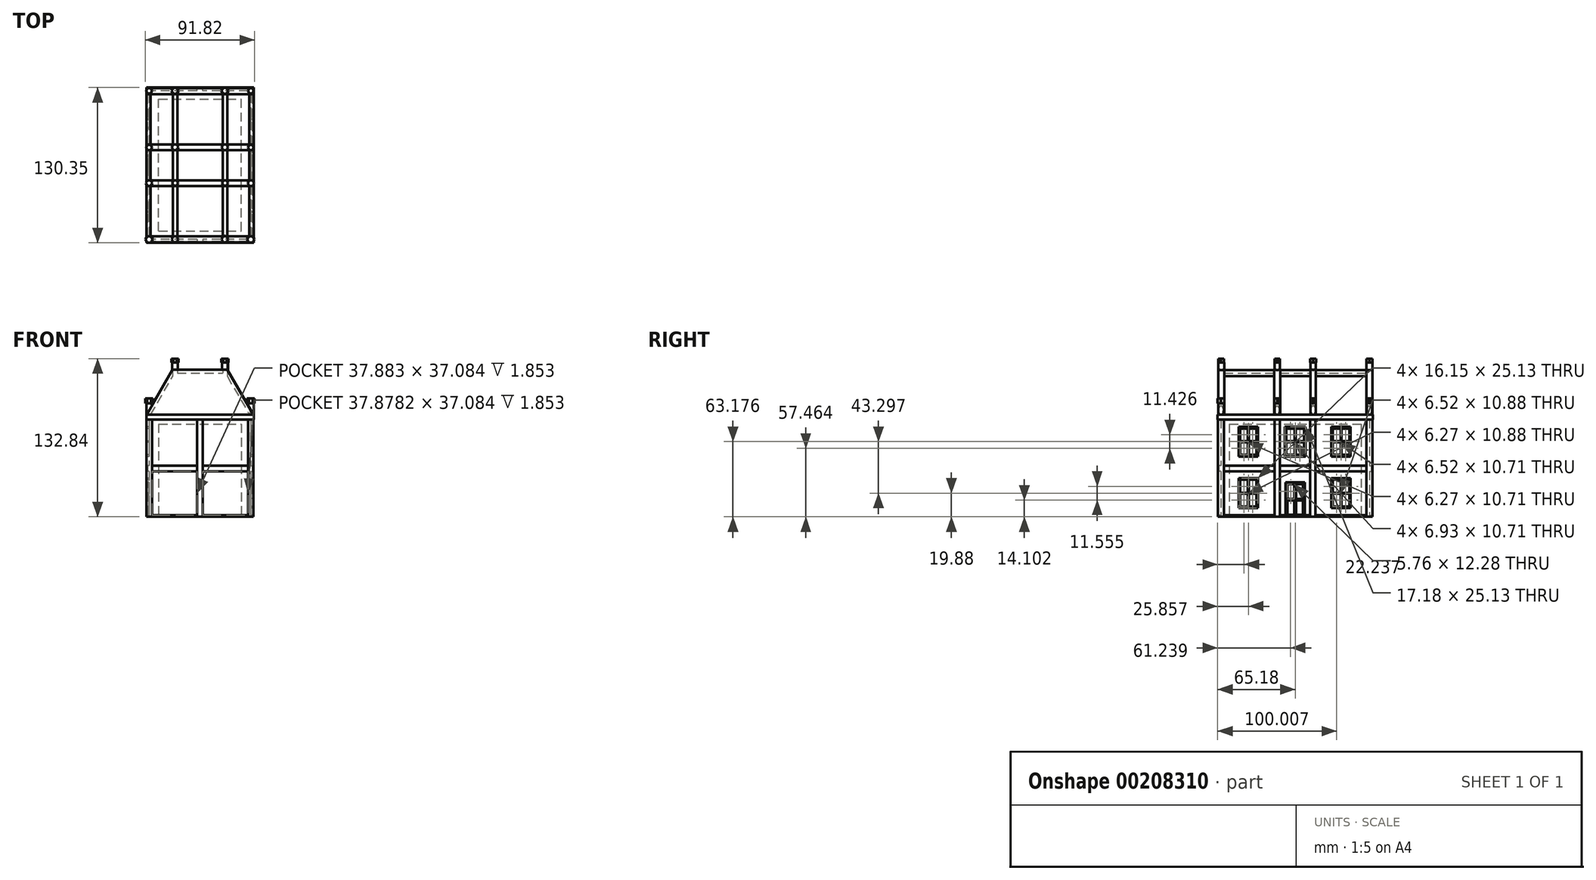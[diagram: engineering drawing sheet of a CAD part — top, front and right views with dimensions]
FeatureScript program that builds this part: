
annotation { "Feature Type Name" : "Feature", "Feature Type Description" : "" }
export const myFeature = defineFeature(function(context is Context, id is Id, definition is map)
    precondition{}
    {
        {
            var Q0;
            Q0=qCreatedBy(makeId("Top.planeOp"),FACE);
            var sketch = newSketch(context, id + "F0", { "sketchPlane" : qUnion([Q0])});
            skLineSegment(sketch, "E0.bottom", {"start": v(42.63, 62.44) * mm, "end": v(-42.63, 62.44) * mm});
            skLineSegment(sketch, "E0.top", {"start": v(42.63, -62.44) * mm, "end": v(-42.63, -62.44) * mm});
            skLineSegment(sketch, "E0.left", {"start": v(42.63, 62.44) * mm, "end": v(42.63, -62.44) * mm});
            skLineSegment(sketch, "E0.right", {"start": v(-42.63, 62.44) * mm, "end": v(-42.63, -62.44) * mm});
            skPoint(sketch, "E0.middle", {"position": v(0, 0) * mm});
            skLineSegment(sketch, "E1.bottom", {"start": v(40.33, -64.96) * mm, "end": v(44.94, -64.96) * mm});
            skLineSegment(sketch, "E1.top", {"start": v(40.33, -59.92) * mm, "end": v(44.94, -59.92) * mm});
            skLineSegment(sketch, "E1.left", {"start": v(40.33, -64.96) * mm, "end": v(40.33, -59.92) * mm});
            skLineSegment(sketch, "E1.right", {"start": v(44.94, -64.96) * mm, "end": v(44.94, -59.92) * mm});
            skPoint(sketch, "E1.middle", {"position": v(42.63, -62.44) * mm});
            skLineSegment(sketch, "E2.bottom", {"start": v(-40.33, -59.92) * mm, "end": v(-44.94, -59.92) * mm});
            skLineSegment(sketch, "E2.top", {"start": v(-40.33, -64.96) * mm, "end": v(-44.94, -64.96) * mm});
            skLineSegment(sketch, "E2.left", {"start": v(-40.33, -59.92) * mm, "end": v(-40.33, -64.96) * mm});
            skLineSegment(sketch, "E2.right", {"start": v(-44.94, -59.92) * mm, "end": v(-44.94, -64.96) * mm});
            skPoint(sketch, "E2.middle", {"position": v(-42.63, -62.44) * mm});
            skLineSegment(sketch, "E3.bottom", {"start": v(-40.33, 59.83) * mm, "end": v(-44.94, 59.83) * mm});
            skLineSegment(sketch, "E3.top", {"start": v(-40.33, 65.05) * mm, "end": v(-44.94, 65.05) * mm});
            skLineSegment(sketch, "E3.left", {"start": v(-40.33, 59.83) * mm, "end": v(-40.33, 65.05) * mm});
            skLineSegment(sketch, "E3.right", {"start": v(-44.94, 59.83) * mm, "end": v(-44.94, 65.05) * mm});
            skPoint(sketch, "E3.middle", {"position": v(-42.63, 62.44) * mm});
            skLineSegment(sketch, "E4.bottom", {"start": v(40.33, 59.83) * mm, "end": v(44.94, 59.83) * mm});
            skLineSegment(sketch, "E4.top", {"start": v(40.33, 65.05) * mm, "end": v(44.94, 65.05) * mm});
            skLineSegment(sketch, "E4.left", {"start": v(40.33, 59.83) * mm, "end": v(40.33, 65.05) * mm});
            skLineSegment(sketch, "E4.right", {"start": v(44.94, 59.83) * mm, "end": v(44.94, 65.05) * mm});
            skPoint(sketch, "E4.middle", {"position": v(42.63, 62.44) * mm});
            skLineSegment(sketch, "E5", {"start": v(40.33, -59.92) * mm, "end": v(0, 0) * mm});
            skLineSegment(sketch, "E6", {"start": v(40.33, 59.83) * mm, "end": v(0, 0) * mm});
            skLineSegment(sketch, "E7", {"start": v(-40.33, 59.83) * mm, "end": v(0, 0) * mm});
            skLineSegment(sketch, "E8", {"start": v(-40.33, -59.92) * mm, "end": v(0, 0) * mm});
            skLineSegment(sketch, "E9", {"start": v(20.16, -29.96) * mm, "end": v(-20.17, -29.96) * mm});
            skLineSegment(sketch, "E10", {"start": v(-20.17, -29.96) * mm, "end": v(-20.17, 29.92) * mm});
            skLineSegment(sketch, "E11", {"start": v(-20.17, 29.92) * mm, "end": v(20.16, 29.92) * mm});
            skLineSegment(sketch, "E12", {"start": v(20.16, 29.92) * mm, "end": v(20.16, -29.96) * mm});
            skPoint(sketch, "E13.middle", {"position": v(42.63, 29.92) * mm});
            skLineSegment(sketch, "E14.bottom", {"start": v(-2.45, -59.92) * mm, "end": v(2.45, -59.92) * mm});
            skLineSegment(sketch, "E14.top", {"start": v(-2.45, -64.96) * mm, "end": v(2.45, -64.96) * mm});
            skLineSegment(sketch, "E14.left", {"start": v(-2.45, -59.92) * mm, "end": v(-2.45, -64.96) * mm});
            skLineSegment(sketch, "E14.right", {"start": v(2.45, -59.92) * mm, "end": v(2.45, -64.96) * mm});
            skPoint(sketch, "E14.middle", {"position": v(0, -62.44) * mm});
            skLineSegment(sketch, "E15.bottom", {"start": v(2.45, 59.83) * mm, "end": v(-2.45, 59.83) * mm});
            skLineSegment(sketch, "E15.top", {"start": v(2.45, 65.05) * mm, "end": v(-2.45, 65.05) * mm});
            skLineSegment(sketch, "E15.left", {"start": v(2.45, 59.83) * mm, "end": v(2.45, 65.05) * mm});
            skLineSegment(sketch, "E15.right", {"start": v(-2.45, 59.83) * mm, "end": v(-2.45, 65.05) * mm});
            skPoint(sketch, "E15.middle", {"position": v(0, 62.44) * mm});
            skPoint(sketch, "E16.middle", {"position": v(-42.63, -29.96) * mm});
            skPoint(sketch, "E17.middle", {"position": v(-42.63, 29.92) * mm});
            skLineSegment(sketch, "E18.bottom", {"start": v(40.33, -17.25) * mm, "end": v(44.94, -17.25) * mm});
            skLineSegment(sketch, "E18.top", {"start": v(40.33, -12.94) * mm, "end": v(44.94, -12.94) * mm});
            skLineSegment(sketch, "E18.left", {"start": v(40.33, -17.25) * mm, "end": v(40.33, -12.94) * mm});
            skLineSegment(sketch, "E18.right", {"start": v(44.94, -17.25) * mm, "end": v(44.94, -12.94) * mm});
            skPoint(sketch, "E18.middle", {"position": v(42.63, -15.1) * mm});
            skLineSegment(sketch, "E19.bottom", {"start": v(40.33, 12.67) * mm, "end": v(44.94, 12.67) * mm});
            skLineSegment(sketch, "E19.top", {"start": v(40.33, 17.11) * mm, "end": v(44.94, 17.11) * mm});
            skLineSegment(sketch, "E19.left", {"start": v(40.33, 12.67) * mm, "end": v(40.33, 17.11) * mm});
            skLineSegment(sketch, "E19.right", {"start": v(44.94, 12.67) * mm, "end": v(44.94, 17.11) * mm});
            skPoint(sketch, "E19.middle", {"position": v(42.63, 14.9) * mm});
            skLineSegment(sketch, "E20.bottom", {"start": v(-40.33, -12.94) * mm, "end": v(-44.94, -12.94) * mm});
            skLineSegment(sketch, "E20.top", {"start": v(-40.33, -17.25) * mm, "end": v(-44.94, -17.25) * mm});
            skLineSegment(sketch, "E20.left", {"start": v(-40.33, -12.94) * mm, "end": v(-40.33, -17.25) * mm});
            skLineSegment(sketch, "E20.right", {"start": v(-44.94, -12.94) * mm, "end": v(-44.94, -17.25) * mm});
            skPoint(sketch, "E20.middle", {"position": v(-42.63, -15.1) * mm});
            skLineSegment(sketch, "E21.bottom", {"start": v(-40.33, 17.11) * mm, "end": v(-44.94, 17.11) * mm});
            skLineSegment(sketch, "E21.top", {"start": v(-40.33, 12.67) * mm, "end": v(-44.94, 12.67) * mm});
            skLineSegment(sketch, "E21.left", {"start": v(-40.33, 17.11) * mm, "end": v(-40.33, 12.67) * mm});
            skLineSegment(sketch, "E21.right", {"start": v(-44.94, 17.11) * mm, "end": v(-44.94, 12.67) * mm});
            skPoint(sketch, "E21.middle", {"position": v(-42.63, 14.9) * mm});
            skPoint(sketch, "E21.middle.positionSnap0", {"position": v(40.33, 14.9) * mm});
            skPoint(sketch, "E21.centerSnap0", {"position": v(40.33, 14.9) * mm});
            skSolve(sketch);
        }
        {
            var Q0;
            Q0 = qSketchRegion(id + "F0", true);
            extrude(context, id + "F1", {"entities" : qUnion([Q0]), "depth" : 83.31 * mm});
        }
        {
            var Q0;
            Q0=qCreatedBy(makeId("Top.planeOp"),FACE);
            var sketch = newSketch(context, id + "F2", { "sketchPlane" : qUnion([Q0])});
            skLineSegment(sketch, "E22.bottom", {"start": v(44.7, 64.75) * mm, "end": v(-44.7, 64.75) * mm});
            skLineSegment(sketch, "E22.top", {"start": v(44.7, -64.75) * mm, "end": v(-44.7, -64.75) * mm});
            skLineSegment(sketch, "E22.left", {"start": v(44.7, 64.75) * mm, "end": v(44.7, -64.75) * mm});
            skLineSegment(sketch, "E22.right", {"start": v(-44.7, 64.75) * mm, "end": v(-44.7, -64.75) * mm});
            skPoint(sketch, "E22.middle", {"position": v(0, 0) * mm});
            skSolve(sketch);
        }
        {
            var Q0;
            Q0 = qSketchRegion(id + "F2", true);
            extrude(context, id + "F3", {"entities" : qUnion([Q0]), "operationType" : NewBodyOperationType.ADD, "depth" : 1.27 * mm});
        }
        {
            var Q0;
            Q0=qCreatedBy(makeId("Top.planeOp"),FACE);
            cPlane(context, id + "F4", {"entities" : qUnion([Q0]), "cplaneType" : CPlaneType.OFFSET, "offset" : 40.64 * mm, "width" : 152.4 * mm, "height" : 152.4 * mm});
        }
        {
            var Q0;
            Q0=qCreatedBy(id+"F4.planeOp",FACE);
            var sketch = newSketch(context, id + "F5", { "sketchPlane" : qUnion([Q0])});
            skLineSegment(sketch, "E23.bottom", {"start": v(44.15, -64.3) * mm, "end": v(-44.15, -64.3) * mm});
            skLineSegment(sketch, "E23.top", {"start": v(44.15, 64.3) * mm, "end": v(-44.15, 64.3) * mm});
            skLineSegment(sketch, "E23.left", {"start": v(44.15, -64.3) * mm, "end": v(44.15, 64.3) * mm});
            skLineSegment(sketch, "E23.right", {"start": v(-44.15, -64.3) * mm, "end": v(-44.15, 64.3) * mm});
            skPoint(sketch, "E23.middle", {"position": v(0, 0) * mm});
            skSolve(sketch);
        }
        {
            var Q0;
            Q0 = qSketchRegion(id + "F5", true);
            extrude(context, id + "F6", {"entities" : qUnion([Q0]), "operationType" : NewBodyOperationType.ADD, "endBound" : BoundingType.SYMMETRIC, "depth" : 4.57 * mm});
        }
        {
            var Q0;
            Q0=qCreatedBy(makeId("Right.planeOp"),FACE);
            var sketch = newSketch(context, id + "F7", { "sketchPlane" : qUnion([Q0])});
            skLineSegment(sketch, "E24.bottom", {"start": v(30.45, 32.44) * mm, "end": v(46.6, 32.44) * mm});
            skLineSegment(sketch, "E24.top", {"start": v(30.45, 7.32) * mm, "end": v(46.6, 7.32) * mm});
            skLineSegment(sketch, "E24.left", {"start": v(30.45, 32.44) * mm, "end": v(30.45, 7.32) * mm});
            skLineSegment(sketch, "E24.right", {"start": v(46.6, 32.44) * mm, "end": v(46.6, 7.32) * mm});
            skPoint(sketch, "E24.middle", {"position": v(38.52, 19.88) * mm});
            skLineSegment(sketch, "E25.bottom", {"start": v(-31.25, 32.44) * mm, "end": v(-47.4, 32.44) * mm});
            skLineSegment(sketch, "E25.top", {"start": v(-31.25, 7.32) * mm, "end": v(-47.4, 7.32) * mm});
            skLineSegment(sketch, "E25.left", {"start": v(-31.25, 32.44) * mm, "end": v(-31.25, 7.32) * mm});
            skLineSegment(sketch, "E25.right", {"start": v(-47.4, 32.44) * mm, "end": v(-47.4, 7.32) * mm});
            skPoint(sketch, "E25.middle", {"position": v(-39.32, 19.88) * mm});
            skLineSegment(sketch, "E26.bottom", {"start": v(30.45, 75.74) * mm, "end": v(46.6, 75.74) * mm});
            skLineSegment(sketch, "E26.top", {"start": v(30.45, 50.61) * mm, "end": v(46.6, 50.61) * mm});
            skLineSegment(sketch, "E26.left", {"start": v(30.45, 75.74) * mm, "end": v(30.45, 50.61) * mm});
            skLineSegment(sketch, "E26.right", {"start": v(46.6, 75.74) * mm, "end": v(46.6, 50.61) * mm});
            skPoint(sketch, "E26.middle", {"position": v(38.52, 63.18) * mm});
            skPoint(sketch, "E26.cornerSnap0", {"position": v(30.45, 19.88) * mm});
            skLineSegment(sketch, "E27.bottom", {"start": v(-31.25, 50.61) * mm, "end": v(-47.4, 50.61) * mm});
            skLineSegment(sketch, "E27.top", {"start": v(-31.25, 75.74) * mm, "end": v(-47.4, 75.74) * mm});
            skLineSegment(sketch, "E27.left", {"start": v(-31.25, 50.61) * mm, "end": v(-31.25, 75.74) * mm});
            skLineSegment(sketch, "E27.right", {"start": v(-47.4, 50.61) * mm, "end": v(-47.4, 75.74) * mm});
            skPoint(sketch, "E27.middle", {"position": v(-39.32, 63.18) * mm});
            skPoint(sketch, "E27.middle.positionSnap0", {"position": v(-39.32, 32.44) * mm});
            skPoint(sketch, "E27.centerSnap0", {"position": v(-39.32, 32.44) * mm});
            skLineSegment(sketch, "E28.bottom", {"start": v(-8.59, 50.61) * mm, "end": v(8.59, 50.61) * mm});
            skLineSegment(sketch, "E28.top", {"start": v(-8.59, 75.74) * mm, "end": v(8.59, 75.74) * mm});
            skLineSegment(sketch, "E28.left", {"start": v(-8.59, 50.61) * mm, "end": v(-8.59, 75.74) * mm});
            skLineSegment(sketch, "E28.right", {"start": v(8.59, 50.61) * mm, "end": v(8.59, 75.74) * mm});
            skPoint(sketch, "E28.middle", {"position": v(0, 63.18) * mm});
            skLineSegment(sketch, "E29.left", {"start": v(-39.8, 8.66) * mm, "end": v(-39.8, 31.1) * mm});
            skLineSegment(sketch, "E29.right", {"start": v(-38.84, 8.66) * mm, "end": v(-38.84, 31.1) * mm});
            skLineSegment(sketch, "E30.left", {"start": v(-39.8, 52.1) * mm, "end": v(-39.8, 74.25) * mm});
            skLineSegment(sketch, "E30.right", {"start": v(-38.84, 52.1) * mm, "end": v(-38.84, 74.25) * mm});
            skLineSegment(sketch, "E31.left", {"start": v(-0.47, 52.1) * mm, "end": v(-0.47, 74.25) * mm});
            skLineSegment(sketch, "E31.right", {"start": v(0.47, 52.1) * mm, "end": v(0.47, 74.25) * mm});
            skLineSegment(sketch, "E32.left", {"start": v(38.09, 52.1) * mm, "end": v(38.09, 74.25) * mm});
            skLineSegment(sketch, "E32.right", {"start": v(38.96, 52.1) * mm, "end": v(38.96, 74.25) * mm});
            skLineSegment(sketch, "E33.left", {"start": v(38.96, 31.1) * mm, "end": v(38.96, 8.66) * mm});
            skLineSegment(sketch, "E33.right", {"start": v(38.09, 31.1) * mm, "end": v(38.09, 8.66) * mm});
            skLineSegment(sketch, "E34.bottom", {"start": v(31.57, 20.22) * mm, "end": v(45.48, 20.22) * mm});
            skLineSegment(sketch, "E35.bottom", {"start": v(-32.57, 20.22) * mm, "end": v(-46.08, 20.22) * mm});
            skLineSegment(sketch, "E36.bottom", {"start": v(-32.57, 63.53) * mm, "end": v(-46.08, 63.53) * mm});
            skLineSegment(sketch, "E37.bottom", {"start": v(-7.4, 63.53) * mm, "end": v(7.4, 63.53) * mm});
            skLineSegment(sketch, "E38.bottom", {"start": v(31.57, 63.53) * mm, "end": v(45.48, 63.53) * mm});
            skLineSegment(sketch, "E39", {"start": v(-46.08, 19.54) * mm, "end": v(-46.08, 8.66) * mm});
            skLineSegment(sketch, "E40", {"start": v(-32.57, 19.54) * mm, "end": v(-32.57, 8.66) * mm});
            skLineSegment(sketch, "E41", {"start": v(-32.57, 20.22) * mm, "end": v(-32.57, 31.1) * mm});
            skLineSegment(sketch, "E42", {"start": v(-46.08, 31.1) * mm, "end": v(-46.08, 20.22) * mm});
            skLineSegment(sketch, "E43", {"start": v(-32.57, 8.66) * mm, "end": v(-38.84, 8.66) * mm});
            skLineSegment(sketch, "E44", {"start": v(-39.8, 8.66) * mm, "end": v(-46.08, 8.66) * mm});
            skLineSegment(sketch, "E45", {"start": v(-32.57, 31.1) * mm, "end": v(-38.84, 31.1) * mm});
            skLineSegment(sketch, "E46", {"start": v(-39.8, 31.1) * mm, "end": v(-46.08, 31.1) * mm});
            skLineSegment(sketch, "E47", {"start": v(38.09, 8.66) * mm, "end": v(31.57, 8.66) * mm});
            skLineSegment(sketch, "E48", {"start": v(38.96, 8.66) * mm, "end": v(45.48, 8.66) * mm});
            skLineSegment(sketch, "E49", {"start": v(38.09, 31.1) * mm, "end": v(31.57, 31.1) * mm});
            skLineSegment(sketch, "E50", {"start": v(38.96, 31.1) * mm, "end": v(45.48, 31.1) * mm});
            skLineSegment(sketch, "E51", {"start": v(31.57, 31.1) * mm, "end": v(31.57, 20.22) * mm});
            skLineSegment(sketch, "E52", {"start": v(45.48, 20.22) * mm, "end": v(45.48, 31.1) * mm});
            skLineSegment(sketch, "E53", {"start": v(31.57, 19.54) * mm, "end": v(31.57, 8.66) * mm});
            skLineSegment(sketch, "E54", {"start": v(45.48, 8.66) * mm, "end": v(45.48, 19.54) * mm});
            skLineSegment(sketch, "E55", {"start": v(31.57, 19.54) * mm, "end": v(38.09, 19.54) * mm});
            skLineSegment(sketch, "E56", {"start": v(45.48, 19.54) * mm, "end": v(38.96, 19.54) * mm});
            skLineSegment(sketch, "E57", {"start": v(-46.08, 19.54) * mm, "end": v(-39.8, 19.54) * mm});
            skLineSegment(sketch, "E58", {"start": v(-32.57, 19.54) * mm, "end": v(-38.84, 19.54) * mm});
            skLineSegment(sketch, "E59", {"start": v(-46.08, 52.1) * mm, "end": v(-39.8, 52.1) * mm});
            skLineSegment(sketch, "E60", {"start": v(-38.84, 52.1) * mm, "end": v(-32.57, 52.1) * mm});
            skLineSegment(sketch, "E61", {"start": v(-7.4, 52.1) * mm, "end": v(-0.47, 52.1) * mm});
            skLineSegment(sketch, "E62", {"start": v(0.47, 52.1) * mm, "end": v(7.4, 52.1) * mm});
            skLineSegment(sketch, "E63", {"start": v(31.57, 52.1) * mm, "end": v(38.09, 52.1) * mm});
            skLineSegment(sketch, "E64", {"start": v(38.96, 52.1) * mm, "end": v(45.48, 52.1) * mm});
            skLineSegment(sketch, "E65", {"start": v(-46.08, 74.25) * mm, "end": v(-39.8, 74.25) * mm});
            skLineSegment(sketch, "E66", {"start": v(-38.84, 74.25) * mm, "end": v(-32.57, 74.25) * mm});
            skLineSegment(sketch, "E67", {"start": v(-7.4, 74.25) * mm, "end": v(-0.47, 74.25) * mm});
            skLineSegment(sketch, "E68", {"start": v(0.47, 74.25) * mm, "end": v(7.4, 74.25) * mm});
            skLineSegment(sketch, "E69", {"start": v(31.57, 74.25) * mm, "end": v(38.09, 74.25) * mm});
            skLineSegment(sketch, "E70", {"start": v(38.96, 74.25) * mm, "end": v(45.48, 74.25) * mm});
            skLineSegment(sketch, "E71", {"start": v(31.57, 62.82) * mm, "end": v(38.09, 62.82) * mm});
            skLineSegment(sketch, "E72", {"start": v(45.48, 62.82) * mm, "end": v(38.96, 62.82) * mm});
            skLineSegment(sketch, "E73", {"start": v(31.57, 74.25) * mm, "end": v(31.57, 63.53) * mm});
            skLineSegment(sketch, "E74", {"start": v(45.48, 74.25) * mm, "end": v(45.48, 63.53) * mm});
            skLineSegment(sketch, "E75", {"start": v(45.48, 52.1) * mm, "end": v(45.48, 62.82) * mm});
            skLineSegment(sketch, "E76", {"start": v(31.57, 62.82) * mm, "end": v(31.57, 52.1) * mm});
            skLineSegment(sketch, "E77", {"start": v(-7.4, 62.82) * mm, "end": v(-7.4, 52.1) * mm});
            skLineSegment(sketch, "E78", {"start": v(7.4, 52.1) * mm, "end": v(7.4, 62.82) * mm});
            skLineSegment(sketch, "E79", {"start": v(-7.4, 62.82) * mm, "end": v(-0.47, 62.82) * mm});
            skLineSegment(sketch, "E80", {"start": v(7.4, 62.82) * mm, "end": v(0.47, 62.82) * mm});
            skLineSegment(sketch, "E81", {"start": v(7.4, 63.53) * mm, "end": v(7.4, 74.25) * mm});
            skLineSegment(sketch, "E82", {"start": v(-7.4, 63.53) * mm, "end": v(-7.4, 74.25) * mm});
            skLineSegment(sketch, "E83", {"start": v(-46.08, 52.1) * mm, "end": v(-46.08, 62.82) * mm});
            skLineSegment(sketch, "E84", {"start": v(-32.57, 52.1) * mm, "end": v(-32.57, 62.82) * mm});
            skLineSegment(sketch, "E85", {"start": v(-32.57, 63.53) * mm, "end": v(-32.57, 74.25) * mm});
            skLineSegment(sketch, "E86", {"start": v(-46.08, 63.53) * mm, "end": v(-46.08, 74.25) * mm});
            skLineSegment(sketch, "E87", {"start": v(-46.08, 62.82) * mm, "end": v(-39.8, 62.82) * mm});
            skLineSegment(sketch, "E88", {"start": v(-32.57, 62.82) * mm, "end": v(-38.84, 62.82) * mm});
            skSolve(sketch);
        }
        {
            var Q0;
            Q0 = qSketchRegion(id + "F7", true);
            extrude(context, id + "F8", {"entities" : qUnion([Q0]), "operationType" : NewBodyOperationType.ADD, "endBound" : BoundingType.SYMMETRIC, "depth" : 89.4 * mm});
        }
        {
            var Q0;
            Q0 = qSketchRegion(id + "F7", true);
            extrude(context, id + "F9", {"entities" : qUnion([Q0]), "operationType" : NewBodyOperationType.ADD, "depth" : 25.4 * mm});
        }
        {
            var Q0;
            Q0 = qSketchRegion(id + "F7", true);
            extrude(context, id + "F10", {"entities" : qUnion([Q0]), "operationType" : NewBodyOperationType.ADD, "depth" : 25.4 * mm});
        }
        {
            var Q0;
            Q0=qCreatedBy(id+"F4.planeOp",FACE);
            cPlane(context, id + "F11", {"entities" : qUnion([Q0]), "cplaneType" : CPlaneType.OFFSET, "offset" : 43.18 * mm, "width" : 152.4 * mm, "height" : 152.4 * mm});
        }
        {
            var Q0;
            Q0=qCreatedBy(id+"F11.planeOp",FACE);
            var sketch = newSketch(context, id + "F12", { "sketchPlane" : qUnion([Q0])});
            skLineSegment(sketch, "E89.bottom", {"start": v(45.1, 65.17) * mm, "end": v(-45.1, 65.17) * mm});
            skLineSegment(sketch, "E89.top", {"start": v(45.1, -65.17) * mm, "end": v(-45.1, -65.17) * mm});
            skLineSegment(sketch, "E89.left", {"start": v(45.1, 65.17) * mm, "end": v(45.1, -65.17) * mm});
            skLineSegment(sketch, "E89.right", {"start": v(-45.1, 65.17) * mm, "end": v(-45.1, -65.17) * mm});
            skPoint(sketch, "E89.middle", {"position": v(0, 0) * mm});
            skSolve(sketch);
        }
        {
            var Q0;
            Q0 = qSketchRegion(id + "F12", true);
            extrude(context, id + "F13", {"entities" : qUnion([Q0]), "operationType" : NewBodyOperationType.ADD, "endBound" : BoundingType.SYMMETRIC, "depth" : 4.06 * mm});
        }
        {
            var Q0;
            Q0=qCreatedBy(makeId("Front.planeOp"),FACE);
            var sketch = newSketch(context, id + "F14", { "sketchPlane" : qUnion([Q0])});
            skCircle(sketch, "E90.cCircle", {"center": v(0, 83.84) * mm, "radius": 36.97 * mm, "construction": true});
            skLineSegment(sketch, "E90.0", {"start": v(21.35, 46.87) * mm, "end": v(-21.35, 46.87) * mm});
            skLineSegment(sketch, "E90.1", {"start": v(-21.35, 46.87) * mm, "end": v(-42.7, 83.84) * mm});
            skLineSegment(sketch, "E90.2", {"start": v(-42.7, 83.84) * mm, "end": v(-21.35, 120.82) * mm});
            skLineSegment(sketch, "E90.3", {"start": v(-21.35, 120.82) * mm, "end": v(21.35, 120.82) * mm});
            skLineSegment(sketch, "E90.4", {"start": v(21.35, 120.82) * mm, "end": v(42.7, 83.84) * mm});
            skLineSegment(sketch, "E90.5", {"start": v(42.7, 83.84) * mm, "end": v(21.35, 46.87) * mm});
            skPoint(sketch, "E90.0.midPoint", {"position": v(0, 46.87) * mm});
            skSolve(sketch);
        }
        {
            var Q0;
            Q0 = qSketchRegion(id + "F14", true);
            extrude(context, id + "F15", {"entities" : qUnion([Q0]), "operationType" : NewBodyOperationType.ADD, "endBound" : BoundingType.SYMMETRIC, "depth" : 123.95 * mm});
        }
        {
            var Q0;
            Q0=qCreatedBy(makeId("Front.planeOp"),FACE);
            cPlane(context, id + "F16", {"entities" : qUnion([Q0]), "cplaneType" : CPlaneType.OFFSET, "offset" : 64.77 * mm, "width" : 152.4 * mm, "height" : 152.4 * mm});
        }
        {
            var Q0;
            Q0=qCreatedBy(id+"F16.planeOp",FACE);
            var sketch = newSketch(context, id + "F17", { "sketchPlane" : qUnion([Q0])});
            skLineSegment(sketch, "E91.0", {"start": v(-22.93, 123.62) * mm, "end": v(22.93, 123.62) * mm});
            skLineSegment(sketch, "E91.1", {"start": v(22.93, 123.62) * mm, "end": v(45.85, 83.91) * mm});
            skLineSegment(sketch, "E91.5", {"start": v(-45.85, 83.91) * mm, "end": v(-22.93, 123.62) * mm});
            skPoint(sketch, "E91.0.midPoint", {"position": v(0, 123.62) * mm});
            skLineSegment(sketch, "E92", {"start": v(-44.92, 85.51) * mm, "end": v(44.92, 85.51) * mm});
            skSolve(sketch);
        }
        {
            var Q0;
            Q0 = qSketchRegion(id + "F17", true);
            extrude(context, id + "F18", {"entities" : qUnion([Q0]), "operationType" : NewBodyOperationType.ADD, "oppositeDirection" : true, "depth" : 5.08 * mm});
        }
        {
            var Q0;
            Q0=qCreatedBy(makeId("Front.planeOp"),FACE);
            cPlane(context, id + "F19", {"entities" : qUnion([Q0]), "cplaneType" : CPlaneType.OFFSET, "offset" : 64.77 * mm, "oppositeDirection" : true, "width" : 152.4 * mm, "height" : 152.4 * mm});
        }
        {
            var Q0;
            Q0=qCreatedBy(id+"F19.planeOp",FACE);
            var sketch = newSketch(context, id + "F20", { "sketchPlane" : qUnion([Q0])});
            skLineSegment(sketch, "E93.0", {"start": v(-22.98, 123.6) * mm, "end": v(22.98, 123.6) * mm});
            skLineSegment(sketch, "E93.1", {"start": v(22.98, 123.6) * mm, "end": v(45.96, 83.8) * mm});
            skLineSegment(sketch, "E93.5", {"start": v(-45.96, 83.8) * mm, "end": v(-22.98, 123.6) * mm});
            skPoint(sketch, "E93.0.midPoint", {"position": v(0, 123.6) * mm});
            skLineSegment(sketch, "E94", {"start": v(44.8, 85.82) * mm, "end": v(-44.8, 85.82) * mm});
            skSolve(sketch);
        }
        {
            var Q0;
            Q0 = qSketchRegion(id + "F20", true);
            extrude(context, id + "F21", {"entities" : qUnion([Q0]), "operationType" : NewBodyOperationType.ADD, "depth" : 5.08 * mm});
        }
        {
            var Q0;
            Q0=qCreatedBy(id+"F11.planeOp",FACE);
            cPlane(context, id + "F22", {"entities" : qUnion([Q0]), "cplaneType" : CPlaneType.OFFSET, "offset" : 39.37 * mm, "width" : 152.4 * mm, "height" : 152.4 * mm});
        }
        {
            var Q0;
            Q0=qCreatedBy(id+"F22.planeOp",FACE);
            var sketch = newSketch(context, id + "F23", { "sketchPlane" : qUnion([Q0])});
            skLineSegment(sketch, "E95.left", {"start": v(-22.88, -60) * mm, "end": v(-22.88, 60) * mm});
            skLineSegment(sketch, "E95.right", {"start": v(22.88, -60) * mm, "end": v(22.88, 60) * mm});
            skPoint(sketch, "E95.middle", {"position": v(0, 0) * mm});
            skLineSegment(sketch, "E96.left", {"start": v(-19.07, -60) * mm, "end": v(-19.07, 60) * mm});
            skLineSegment(sketch, "E96.right", {"start": v(19.07, -60) * mm, "end": v(19.07, 60) * mm});
            skLineSegment(sketch, "E97", {"start": v(22.88, -60) * mm, "end": v(19.07, -60) * mm});
            skLineSegment(sketch, "E98", {"start": v(22.88, 60) * mm, "end": v(19.07, 60) * mm});
            skLineSegment(sketch, "E99", {"start": v(-19.07, 60) * mm, "end": v(-22.88, 60) * mm});
            skLineSegment(sketch, "E100", {"start": v(-19.07, -60) * mm, "end": v(-22.88, -60) * mm});
            skSolve(sketch);
        }
        {
            var Q0;
            Q0 = qSketchRegion(id + "F23", true);
            extrude(context, id + "F24", {"entities" : qUnion([Q0]), "operationType" : NewBodyOperationType.ADD, "oppositeDirection" : true, "depth" : 1.02 * mm});
        }
        {
            var Q0;
            Q0 = qSketchRegion(id + "F23", true);
            extrude(context, id + "F25", {"entities" : qUnion([Q0]), "operationType" : NewBodyOperationType.ADD, "oppositeDirection" : true, "depth" : 12.45 * mm});
        }
        {
            var Q0;
            Q0=qCreatedBy(makeId("Front.planeOp"),FACE);
            cPlane(context, id + "F26", {"entities" : qUnion([Q0]), "cplaneType" : CPlaneType.OFFSET, "offset" : 17.53 * mm, "width" : 152.4 * mm, "height" : 152.4 * mm});
        }
        {
            var Q0;
            Q0=qCreatedBy(makeId("Front.planeOp"),FACE);
            cPlane(context, id + "F27", {"entities" : qUnion([Q0]), "cplaneType" : CPlaneType.OFFSET, "offset" : 17.27 * mm, "oppositeDirection" : true, "width" : 152.4 * mm, "height" : 152.4 * mm});
        }
        {
            var Q0;
            Q0=qCreatedBy(id+"F26.planeOp",FACE);
            var sketch = newSketch(context, id + "F28", { "sketchPlane" : qUnion([Q0])});
            skLineSegment(sketch, "E101.2", {"start": v(-45.74, 83.98) * mm, "end": v(-22.87, 123.6) * mm});
            skLineSegment(sketch, "E101.3", {"start": v(-22.87, 123.6) * mm, "end": v(22.87, 123.6) * mm});
            skLineSegment(sketch, "E101.4", {"start": v(22.87, 123.6) * mm, "end": v(45.74, 83.98) * mm});
            skPoint(sketch, "E101.0.midPoint", {"position": v(0, 44.37) * mm});
            skLineSegment(sketch, "E102", {"start": v(-44.65, 85.88) * mm, "end": v(44.65, 85.88) * mm});
            skSolve(sketch);
        }
        {
            var Q0;
            Q0 = qSketchRegion(id + "F28", true);
            extrude(context, id + "F29", {"entities" : qUnion([Q0]), "operationType" : NewBodyOperationType.ADD, "oppositeDirection" : true, "depth" : 4.83 * mm});
        }
        {
            var Q0;
            Q0=qCreatedBy(id+"F27.planeOp",FACE);
            var sketch = newSketch(context, id + "F30", { "sketchPlane" : qUnion([Q0])});
            skLineSegment(sketch, "E103.0", {"start": v(-22.98, 123.72) * mm, "end": v(22.98, 123.72) * mm});
            skLineSegment(sketch, "E103.1", {"start": v(22.98, 123.72) * mm, "end": v(45.96, 83.92) * mm});
            skPoint(sketch, "E103.0.midPoint", {"position": v(0, 123.72) * mm});
            skLineSegment(sketch, "E104", {"start": v(-44.95, 85.68) * mm, "end": v(44.95, 85.68) * mm});
            skLineSegment(sketch, "E105", {"start": v(-22.98, 123.72) * mm, "end": v(-44.95, 85.68) * mm});
            skSolve(sketch);
        }
        {
            var Q0;
            Q0 = qSketchRegion(id + "F30", true);
            extrude(context, id + "F31", {"entities" : qUnion([Q0]), "operationType" : NewBodyOperationType.ADD, "depth" : 4.57 * mm});
        }
        {
            var Q0;
            Q0=qCreatedBy(makeId("Right.planeOp"),FACE);
            var sketch = newSketch(context, id + "F32", { "sketchPlane" : qUnion([Q0])});
            skLineSegment(sketch, "E106.top", {"start": v(-8.16, 29.03) * mm, "end": v(8.16, 29.03) * mm});
            skLineSegment(sketch, "E106.left", {"start": v(-8.16, 1.21) * mm, "end": v(-8.16, 29.03) * mm});
            skLineSegment(sketch, "E106.right", {"start": v(8.16, 1.21) * mm, "end": v(8.16, 29.03) * mm});
            skPoint(sketch, "E106.middle", {"position": v(0, 15.12) * mm});
            skLineSegment(sketch, "E107.bottom", {"start": v(6.76, 27.86) * mm, "end": v(-6.76, 27.86) * mm});
            skLineSegment(sketch, "E107.left", {"start": v(6.76, 27.86) * mm, "end": v(6.76, 2.39) * mm});
            skLineSegment(sketch, "E107.right", {"start": v(-6.76, 27.86) * mm, "end": v(-6.76, 2.39) * mm});
            skLineSegment(sketch, "E108", {"start": v(6.76, 2.39) * mm, "end": v(6.76, 1.21) * mm});
            skLineSegment(sketch, "E109", {"start": v(6.76, 1.21) * mm, "end": v(8.16, 1.21) * mm});
            skLineSegment(sketch, "E110", {"start": v(-6.76, 2.39) * mm, "end": v(-6.76, 1.21) * mm});
            skLineSegment(sketch, "E111", {"start": v(-6.76, 1.21) * mm, "end": v(-8.16, 1.21) * mm});
            skSolve(sketch);
        }
        {
            var Q0;
            Q0 = qSketchRegion(id + "F32", true);
            extrude(context, id + "F33", {"entities" : qUnion([Q0]), "operationType" : NewBodyOperationType.ADD, "endBound" : BoundingType.SYMMETRIC, "depth" : 89.4 * mm});
        }
        {
            var Q0;
            Q0 = qSketchRegion(id + "F32", true);
            extrude(context, id + "F34", {"entities" : qUnion([Q0]), "operationType" : NewBodyOperationType.ADD, "depth" : 25.4 * mm});
        }
        {
            var Q0;
            Q0=qCreatedBy(makeId("Right.planeOp"),FACE);
            var sketch = newSketch(context, id + "F35", { "sketchPlane" : qUnion([Q0])});
            skLineSegment(sketch, "E112.bottom", {"start": v(-0.07, 1.25) * mm, "end": v(0.07, 1.25) * mm});
            skLineSegment(sketch, "E112.top", {"start": v(-0.07, 27.75) * mm, "end": v(0.07, 27.75) * mm});
            skLineSegment(sketch, "E112.left", {"start": v(-0.07, 1.25) * mm, "end": v(-0.07, 27.75) * mm});
            skLineSegment(sketch, "E112.right", {"start": v(0.07, 1.25) * mm, "end": v(0.07, 27.75) * mm});
            skPoint(sketch, "E112.middle", {"position": v(0, 14.5) * mm});
            skLineSegment(sketch, "E113.bottom", {"start": v(0.07, 27.9) * mm, "end": v(-0.07, 27.9) * mm});
            skLineSegment(sketch, "E113.top", {"start": v(0.07, 27.58) * mm, "end": v(-0.07, 27.58) * mm});
            skLineSegment(sketch, "E113.left", {"start": v(0.07, 27.9) * mm, "end": v(0.07, 27.58) * mm});
            skLineSegment(sketch, "E113.right", {"start": v(-0.07, 27.9) * mm, "end": v(-0.07, 27.58) * mm});
            skPoint(sketch, "E113.middle", {"position": v(0, 27.75) * mm});
            skLineSegment(sketch, "E114.bottom", {"start": v(-0.73, 14.5) * mm, "end": v(0.73, 14.5) * mm});
            skLineSegment(sketch, "E114.top", {"start": v(-0.73, 14.5) * mm, "end": v(0.73, 14.5) * mm});
            skLineSegment(sketch, "E114.left", {"start": v(-0.73, 14.5) * mm, "end": v(-0.73, 14.5) * mm});
            skLineSegment(sketch, "E114.right", {"start": v(0.73, 14.5) * mm, "end": v(0.73, 14.5) * mm});
            skCircle(sketch, "E115", {"center": v(-0.73, 14.5) * mm, "radius": 0.27 * mm});
            skCircle(sketch, "E116", {"center": v(0.73, 14.5) * mm, "radius": 0.27 * mm});
            skLineSegment(sketch, "E117.bottom", {"start": v(-6.5, 27.41) * mm, "end": v(-0.66, 27.41) * mm});
            skLineSegment(sketch, "E117.left", {"start": v(-6.5, 27.41) * mm, "end": v(-6.5, 15.13) * mm});
            skLineSegment(sketch, "E118.bottom", {"start": v(-6.5, 1.67) * mm, "end": v(-0.73, 1.67) * mm});
            skLineSegment(sketch, "E118.top", {"start": v(-6.5, 13.73) * mm, "end": v(-0.73, 13.73) * mm});
            skLineSegment(sketch, "E118.left", {"start": v(-6.5, 1.67) * mm, "end": v(-6.5, 13.73) * mm});
            skLineSegment(sketch, "E118.right", {"start": v(-0.73, 1.67) * mm, "end": v(-0.73, 13.73) * mm});
            skLineSegment(sketch, "E119.bottom", {"start": v(6.46, 27.41) * mm, "end": v(0.8, 27.41) * mm});
            skLineSegment(sketch, "E119.top", {"start": v(6.46, 15.13) * mm, "end": v(0.8, 15.13) * mm});
            skLineSegment(sketch, "E119.left", {"start": v(6.46, 27.41) * mm, "end": v(6.46, 15.13) * mm});
            skLineSegment(sketch, "E119.right", {"start": v(0.8, 27.41) * mm, "end": v(0.8, 15.13) * mm});
            skLineSegment(sketch, "E120.bottom", {"start": v(6.46, 1.67) * mm, "end": v(0.8, 1.67) * mm});
            skLineSegment(sketch, "E120.top", {"start": v(6.46, 13.73) * mm, "end": v(0.8, 13.73) * mm});
            skLineSegment(sketch, "E120.left", {"start": v(6.46, 1.67) * mm, "end": v(6.46, 13.73) * mm});
            skLineSegment(sketch, "E120.right", {"start": v(0.8, 1.67) * mm, "end": v(0.8, 13.73) * mm});
            skLineSegment(sketch, "E121.bottom", {"start": v(-6.5, 27.41) * mm, "end": v(-0.73, 27.41) * mm});
            skLineSegment(sketch, "E121.top", {"start": v(-6.5, 15.13) * mm, "end": v(-0.73, 15.13) * mm});
            skLineSegment(sketch, "E121.right", {"start": v(-0.73, 27.41) * mm, "end": v(-0.73, 15.13) * mm});
            skSolve(sketch);
        }
        {
            var Q0;
            Q0 = qSketchRegion(id + "F35", true);
            extrude(context, id + "F36", {"entities" : qUnion([Q0]), "operationType" : NewBodyOperationType.ADD, "endBound" : BoundingType.SYMMETRIC, "depth" : 85.85 * mm});
        }
        {
            var Q0;
            Q0=qCreatedBy(id+"F22.planeOp",FACE);
            var sketch = newSketch(context, id + "F37", { "sketchPlane" : qUnion([Q0])});
            skCircle(sketch, "E122", {"center": v(20.92, 62.33) * mm, "radius": 2.55 * mm});
            skCircle(sketch, "E123", {"center": v(-21.02, 62.33) * mm, "radius": 2.38 * mm});
            skCircle(sketch, "E124", {"center": v(-21.02, 15.02) * mm, "radius": 2.27 * mm});
            skCircle(sketch, "E125", {"center": v(20.92, 15.02) * mm, "radius": 2.2 * mm});
            skCircle(sketch, "E126", {"center": v(20.92, -15.14) * mm, "radius": 2.24 * mm});
            skCircle(sketch, "E127", {"center": v(-21.02, -15.14) * mm, "radius": 2.22 * mm});
            skCircle(sketch, "E128", {"center": v(20.92, -62.05) * mm, "radius": 2.45 * mm});
            skCircle(sketch, "E129", {"center": v(-21.02, -62.05) * mm, "radius": 2.35 * mm});
            skSolve(sketch);
        }
        {
            var Q0;
            Q0 = qSketchRegion(id + "F37", true);
            extrude(context, id + "F38", {"entities" : qUnion([Q0]), "operationType" : NewBodyOperationType.ADD, "depth" : 6.35 * mm});
        }
        {
            var Q0;
            Q0=qCreatedBy(id+"F11.planeOp",FACE);
            var sketch = newSketch(context, id + "F39", { "sketchPlane" : qUnion([Q0])});
            skPoint(sketch, "E130.middle", {"position": v(0, 0) * mm});
            skCircle(sketch, "E131", {"center": v(-42.74, -62.37) * mm, "radius": 2.2 * mm});
            skCircle(sketch, "E132", {"center": v(-42.74, -15.18) * mm, "radius": 2.24 * mm});
            skCircle(sketch, "E133", {"center": v(-42.74, 15.09) * mm, "radius": 2.15 * mm});
            skCircle(sketch, "E134", {"center": v(-42.74, 62.37) * mm, "radius": 2.27 * mm});
            skCircle(sketch, "E135", {"center": v(42.74, -62.37) * mm, "radius": 2.35 * mm});
            skCircle(sketch, "E136", {"center": v(42.74, -15.18) * mm, "radius": 2.26 * mm});
            skCircle(sketch, "E137", {"center": v(42.74, 15.09) * mm, "radius": 2.28 * mm});
            skCircle(sketch, "E138", {"center": v(42.74, 62.37) * mm, "radius": 2.25 * mm});
            skSolve(sketch);
        }
        {
            var Q0;
            Q0 = qSketchRegion(id + "F39", true);
            extrude(context, id + "F40", {"entities" : qUnion([Q0]), "operationType" : NewBodyOperationType.ADD, "depth" : 11.94 * mm});
        }
        {
            var Q0;
            Q0=qCreatedBy(id+"F11.planeOp",FACE);
            cPlane(context, id + "F41", {"entities" : qUnion([Q0]), "cplaneType" : CPlaneType.OFFSET, "offset" : 11.68 * mm, "width" : 152.4 * mm, "height" : 152.4 * mm});
        }
        {
            var Q0;
            Q0=qCreatedBy(id+"F41.planeOp",FACE);
            var sketch = newSketch(context, id + "F42", { "sketchPlane" : qUnion([Q0])});
            skPoint(sketch, "E139.middle", {"position": v(0, 0) * mm});
            skCircle(sketch, "E140.cCircle", {"center": v(42.74, 62.44) * mm, "radius": 2.08 * mm, "construction": true});
            skLineSegment(sketch, "E140.0", {"start": v(43.94, 60.36) * mm, "end": v(41.54, 60.36) * mm});
            skLineSegment(sketch, "E140.1", {"start": v(41.54, 60.36) * mm, "end": v(40.34, 62.44) * mm});
            skLineSegment(sketch, "E140.2", {"start": v(40.34, 62.44) * mm, "end": v(41.54, 64.51) * mm});
            skLineSegment(sketch, "E140.3", {"start": v(41.54, 64.51) * mm, "end": v(43.94, 64.51) * mm});
            skLineSegment(sketch, "E140.4", {"start": v(43.94, 64.51) * mm, "end": v(45.14, 62.44) * mm});
            skLineSegment(sketch, "E140.5", {"start": v(45.14, 62.44) * mm, "end": v(43.94, 60.36) * mm});
            skPoint(sketch, "E140.0.midPoint", {"position": v(42.74, 60.36) * mm});
            skCircle(sketch, "E141.cCircle", {"center": v(-42.74, 62.44) * mm, "radius": 2.08 * mm, "construction": true});
            skLineSegment(sketch, "E141.0", {"start": v(-41.54, 60.36) * mm, "end": v(-43.94, 60.36) * mm});
            skLineSegment(sketch, "E141.1", {"start": v(-43.94, 60.36) * mm, "end": v(-45.14, 62.44) * mm});
            skLineSegment(sketch, "E141.2", {"start": v(-45.14, 62.44) * mm, "end": v(-43.94, 64.51) * mm});
            skLineSegment(sketch, "E141.3", {"start": v(-43.94, 64.51) * mm, "end": v(-41.54, 64.51) * mm});
            skLineSegment(sketch, "E141.4", {"start": v(-41.54, 64.51) * mm, "end": v(-40.34, 62.44) * mm});
            skLineSegment(sketch, "E141.5", {"start": v(-40.34, 62.44) * mm, "end": v(-41.54, 60.36) * mm});
            skPoint(sketch, "E141.0.midPoint", {"position": v(-42.74, 60.36) * mm});
            skCircle(sketch, "E142.cCircle", {"center": v(-42.74, 14.85) * mm, "radius": 2.1 * mm, "construction": true});
            skLineSegment(sketch, "E142.0", {"start": v(-43.96, 16.96) * mm, "end": v(-41.53, 16.96) * mm});
            skLineSegment(sketch, "E142.1", {"start": v(-41.53, 16.96) * mm, "end": v(-40.3, 14.85) * mm});
            skLineSegment(sketch, "E142.2", {"start": v(-40.3, 14.85) * mm, "end": v(-41.53, 12.74) * mm});
            skLineSegment(sketch, "E142.3", {"start": v(-41.53, 12.74) * mm, "end": v(-43.96, 12.74) * mm});
            skLineSegment(sketch, "E142.4", {"start": v(-43.96, 12.74) * mm, "end": v(-45.18, 14.85) * mm});
            skLineSegment(sketch, "E142.5", {"start": v(-45.18, 14.85) * mm, "end": v(-43.96, 16.96) * mm});
            skPoint(sketch, "E142.0.midPoint", {"position": v(-42.74, 16.96) * mm});
            skCircle(sketch, "E143.cCircle", {"center": v(42.74, 14.85) * mm, "radius": 2.1 * mm, "construction": true});
            skLineSegment(sketch, "E143.0", {"start": v(41.53, 16.96) * mm, "end": v(43.96, 16.96) * mm});
            skLineSegment(sketch, "E143.1", {"start": v(43.96, 16.96) * mm, "end": v(45.18, 14.85) * mm});
            skLineSegment(sketch, "E143.2", {"start": v(45.18, 14.85) * mm, "end": v(43.96, 12.74) * mm});
            skLineSegment(sketch, "E143.3", {"start": v(43.96, 12.74) * mm, "end": v(41.53, 12.74) * mm});
            skLineSegment(sketch, "E143.4", {"start": v(41.53, 12.74) * mm, "end": v(40.3, 14.85) * mm});
            skLineSegment(sketch, "E143.5", {"start": v(40.3, 14.85) * mm, "end": v(41.53, 16.96) * mm});
            skPoint(sketch, "E143.0.midPoint", {"position": v(42.74, 16.96) * mm});
            skCircle(sketch, "E144.cCircle", {"center": v(42.74, -15.18) * mm, "radius": 2.37 * mm, "construction": true});
            skLineSegment(sketch, "E144.0", {"start": v(41.37, -12.81) * mm, "end": v(44.11, -12.81) * mm});
            skLineSegment(sketch, "E144.1", {"start": v(44.11, -12.81) * mm, "end": v(45.48, -15.18) * mm});
            skLineSegment(sketch, "E144.2", {"start": v(45.48, -15.18) * mm, "end": v(44.11, -17.56) * mm});
            skLineSegment(sketch, "E144.3", {"start": v(44.11, -17.56) * mm, "end": v(41.37, -17.56) * mm});
            skLineSegment(sketch, "E144.4", {"start": v(41.37, -17.56) * mm, "end": v(40, -15.18) * mm});
            skLineSegment(sketch, "E144.5", {"start": v(40, -15.18) * mm, "end": v(41.37, -12.81) * mm});
            skPoint(sketch, "E144.0.midPoint", {"position": v(42.74, -12.81) * mm});
            skCircle(sketch, "E145.cCircle", {"center": v(-42.74, -15.18) * mm, "radius": 2.37 * mm, "construction": true});
            skLineSegment(sketch, "E145.0", {"start": v(-44.11, -12.81) * mm, "end": v(-41.37, -12.81) * mm});
            skLineSegment(sketch, "E145.1", {"start": v(-41.37, -12.81) * mm, "end": v(-40, -15.18) * mm});
            skLineSegment(sketch, "E145.2", {"start": v(-40, -15.18) * mm, "end": v(-41.37, -17.56) * mm});
            skLineSegment(sketch, "E145.3", {"start": v(-41.37, -17.56) * mm, "end": v(-44.11, -17.56) * mm});
            skLineSegment(sketch, "E145.4", {"start": v(-44.11, -17.56) * mm, "end": v(-45.48, -15.18) * mm});
            skLineSegment(sketch, "E145.5", {"start": v(-45.48, -15.18) * mm, "end": v(-44.11, -12.81) * mm});
            skPoint(sketch, "E145.0.midPoint", {"position": v(-42.74, -12.81) * mm});
            skCircle(sketch, "E146.cCircle", {"center": v(-42.74, -62.44) * mm, "radius": 2.75 * mm, "construction": true});
            skLineSegment(sketch, "E146.0", {"start": v(-44.33, -59.69) * mm, "end": v(-41.16, -59.69) * mm});
            skLineSegment(sketch, "E146.1", {"start": v(-41.16, -59.69) * mm, "end": v(-39.57, -62.44) * mm});
            skLineSegment(sketch, "E146.2", {"start": v(-39.57, -62.44) * mm, "end": v(-41.16, -65.18) * mm});
            skLineSegment(sketch, "E146.3", {"start": v(-41.16, -65.18) * mm, "end": v(-44.33, -65.18) * mm});
            skLineSegment(sketch, "E146.4", {"start": v(-44.33, -65.18) * mm, "end": v(-45.91, -62.44) * mm});
            skLineSegment(sketch, "E146.5", {"start": v(-45.91, -62.44) * mm, "end": v(-44.33, -59.69) * mm});
            skPoint(sketch, "E146.0.midPoint", {"position": v(-42.74, -59.69) * mm});
            skCircle(sketch, "E147.cCircle", {"center": v(42.74, -62.44) * mm, "radius": 2.74 * mm, "construction": true});
            skLineSegment(sketch, "E147.0", {"start": v(41.16, -59.7) * mm, "end": v(44.32, -59.7) * mm});
            skLineSegment(sketch, "E147.1", {"start": v(44.32, -59.7) * mm, "end": v(45.9, -62.44) * mm});
            skLineSegment(sketch, "E147.2", {"start": v(45.9, -62.44) * mm, "end": v(44.32, -65.18) * mm});
            skLineSegment(sketch, "E147.3", {"start": v(44.32, -65.18) * mm, "end": v(41.16, -65.18) * mm});
            skLineSegment(sketch, "E147.4", {"start": v(41.16, -65.18) * mm, "end": v(39.58, -62.44) * mm});
            skLineSegment(sketch, "E147.5", {"start": v(39.58, -62.44) * mm, "end": v(41.16, -59.7) * mm});
            skPoint(sketch, "E147.0.midPoint", {"position": v(42.74, -59.7) * mm});
            skSolve(sketch);
        }
        {
            var Q0;
            Q0 = qSketchRegion(id + "F42", true);
            extrude(context, id + "F43", {"entities" : qUnion([Q0]), "operationType" : NewBodyOperationType.ADD, "depth" : 4.06 * mm});
        }
        {
            var Q0;
            Q0=qCreatedBy(id+"F22.planeOp",FACE);
            cPlane(context, id + "F44", {"entities" : qUnion([Q0]), "cplaneType" : CPlaneType.OFFSET, "offset" : 6.35 * mm, "width" : 152.4 * mm, "height" : 152.4 * mm});
        }
        {
            var Q0;
            Q0=qCreatedBy(id+"F44.planeOp",FACE);
            var sketch = newSketch(context, id + "F45", { "sketchPlane" : qUnion([Q0])});
            skPoint(sketch, "E148.middle", {"position": v(0, 0) * mm});
            skCircle(sketch, "E149.cCircle", {"center": v(20.93, -62.36) * mm, "radius": 2.41 * mm, "construction": true});
            skLineSegment(sketch, "E149.0", {"start": v(22.33, -64.77) * mm, "end": v(19.54, -64.77) * mm});
            skLineSegment(sketch, "E149.1", {"start": v(19.54, -64.77) * mm, "end": v(18.15, -62.36) * mm});
            skLineSegment(sketch, "E149.2", {"start": v(18.15, -62.36) * mm, "end": v(19.54, -59.95) * mm});
            skLineSegment(sketch, "E149.3", {"start": v(19.54, -59.95) * mm, "end": v(22.33, -59.95) * mm});
            skLineSegment(sketch, "E149.4", {"start": v(22.33, -59.95) * mm, "end": v(23.72, -62.36) * mm});
            skLineSegment(sketch, "E149.5", {"start": v(23.72, -62.36) * mm, "end": v(22.33, -64.77) * mm});
            skPoint(sketch, "E149.0.midPoint", {"position": v(20.93, -64.77) * mm});
            skCircle(sketch, "E150.cCircle", {"center": v(-20.93, -62.36) * mm, "radius": 2.41 * mm, "construction": true});
            skLineSegment(sketch, "E150.0", {"start": v(-19.54, -64.77) * mm, "end": v(-22.33, -64.77) * mm});
            skLineSegment(sketch, "E150.1", {"start": v(-22.33, -64.77) * mm, "end": v(-23.72, -62.36) * mm});
            skLineSegment(sketch, "E150.2", {"start": v(-23.72, -62.36) * mm, "end": v(-22.33, -59.95) * mm});
            skLineSegment(sketch, "E150.3", {"start": v(-22.33, -59.95) * mm, "end": v(-19.54, -59.95) * mm});
            skLineSegment(sketch, "E150.4", {"start": v(-19.54, -59.95) * mm, "end": v(-18.15, -62.36) * mm});
            skLineSegment(sketch, "E150.5", {"start": v(-18.15, -62.36) * mm, "end": v(-19.54, -64.77) * mm});
            skPoint(sketch, "E150.0.midPoint", {"position": v(-20.93, -64.77) * mm});
            skCircle(sketch, "E151.cCircle", {"center": v(-20.93, 62.36) * mm, "radius": 2.57 * mm, "construction": true});
            skLineSegment(sketch, "E151.0", {"start": v(-22.42, 64.94) * mm, "end": v(-19.45, 64.94) * mm});
            skLineSegment(sketch, "E151.1", {"start": v(-19.45, 64.94) * mm, "end": v(-17.96, 62.36) * mm});
            skLineSegment(sketch, "E151.2", {"start": v(-17.96, 62.36) * mm, "end": v(-19.45, 59.79) * mm});
            skLineSegment(sketch, "E151.3", {"start": v(-19.45, 59.79) * mm, "end": v(-22.42, 59.79) * mm});
            skLineSegment(sketch, "E151.4", {"start": v(-22.42, 59.79) * mm, "end": v(-23.9, 62.36) * mm});
            skLineSegment(sketch, "E151.5", {"start": v(-23.9, 62.36) * mm, "end": v(-22.42, 64.94) * mm});
            skPoint(sketch, "E151.0.midPoint", {"position": v(-20.93, 64.94) * mm});
            skCircle(sketch, "E152.cCircle", {"center": v(20.93, 62.36) * mm, "radius": 2.57 * mm, "construction": true});
            skLineSegment(sketch, "E152.0", {"start": v(19.45, 64.94) * mm, "end": v(22.42, 64.94) * mm});
            skLineSegment(sketch, "E152.1", {"start": v(22.42, 64.94) * mm, "end": v(23.9, 62.36) * mm});
            skLineSegment(sketch, "E152.2", {"start": v(23.9, 62.36) * mm, "end": v(22.42, 59.79) * mm});
            skLineSegment(sketch, "E152.3", {"start": v(22.42, 59.79) * mm, "end": v(19.45, 59.79) * mm});
            skLineSegment(sketch, "E152.4", {"start": v(19.45, 59.79) * mm, "end": v(17.96, 62.36) * mm});
            skLineSegment(sketch, "E152.5", {"start": v(17.96, 62.36) * mm, "end": v(19.45, 64.94) * mm});
            skPoint(sketch, "E152.0.midPoint", {"position": v(20.93, 64.94) * mm});
            skCircle(sketch, "E153.cCircle", {"center": v(20.93, 15.08) * mm, "radius": 2.44 * mm, "construction": true});
            skLineSegment(sketch, "E153.0", {"start": v(19.53, 17.52) * mm, "end": v(22.34, 17.52) * mm});
            skLineSegment(sketch, "E153.1", {"start": v(22.34, 17.52) * mm, "end": v(23.75, 15.08) * mm});
            skLineSegment(sketch, "E153.2", {"start": v(23.75, 15.08) * mm, "end": v(22.34, 12.64) * mm});
            skLineSegment(sketch, "E153.3", {"start": v(22.34, 12.64) * mm, "end": v(19.53, 12.64) * mm});
            skLineSegment(sketch, "E153.4", {"start": v(19.53, 12.64) * mm, "end": v(18.12, 15.08) * mm});
            skLineSegment(sketch, "E153.5", {"start": v(18.12, 15.08) * mm, "end": v(19.53, 17.52) * mm});
            skPoint(sketch, "E153.0.midPoint", {"position": v(20.93, 17.52) * mm});
            skCircle(sketch, "E154.cCircle", {"center": v(-20.93, 15.08) * mm, "radius": 2.44 * mm, "construction": true});
            skLineSegment(sketch, "E154.0", {"start": v(-22.34, 17.52) * mm, "end": v(-19.53, 17.52) * mm});
            skLineSegment(sketch, "E154.1", {"start": v(-19.53, 17.52) * mm, "end": v(-18.12, 15.08) * mm});
            skLineSegment(sketch, "E154.2", {"start": v(-18.12, 15.08) * mm, "end": v(-19.53, 12.64) * mm});
            skLineSegment(sketch, "E154.3", {"start": v(-19.53, 12.64) * mm, "end": v(-22.34, 12.64) * mm});
            skLineSegment(sketch, "E154.4", {"start": v(-22.34, 12.64) * mm, "end": v(-23.75, 15.08) * mm});
            skLineSegment(sketch, "E154.5", {"start": v(-23.75, 15.08) * mm, "end": v(-22.34, 17.52) * mm});
            skPoint(sketch, "E154.0.midPoint", {"position": v(-20.93, 17.52) * mm});
            skCircle(sketch, "E155.cCircle", {"center": v(-20.93, -15.16) * mm, "radius": 2.22 * mm, "construction": true});
            skLineSegment(sketch, "E155.0", {"start": v(-22.21, -12.94) * mm, "end": v(-19.66, -12.94) * mm});
            skLineSegment(sketch, "E155.1", {"start": v(-19.66, -12.94) * mm, "end": v(-18.38, -15.16) * mm});
            skLineSegment(sketch, "E155.2", {"start": v(-18.38, -15.16) * mm, "end": v(-19.66, -17.37) * mm});
            skLineSegment(sketch, "E155.3", {"start": v(-19.66, -17.37) * mm, "end": v(-22.21, -17.37) * mm});
            skLineSegment(sketch, "E155.4", {"start": v(-22.21, -17.37) * mm, "end": v(-23.5, -15.16) * mm});
            skLineSegment(sketch, "E155.5", {"start": v(-23.5, -15.16) * mm, "end": v(-22.21, -12.94) * mm});
            skPoint(sketch, "E155.0.midPoint", {"position": v(-20.93, -12.94) * mm});
            skCircle(sketch, "E156.cCircle", {"center": v(20.93, -15.16) * mm, "radius": 2.22 * mm, "construction": true});
            skLineSegment(sketch, "E156.0", {"start": v(19.66, -12.94) * mm, "end": v(22.21, -12.94) * mm});
            skLineSegment(sketch, "E156.1", {"start": v(22.21, -12.94) * mm, "end": v(23.5, -15.16) * mm});
            skLineSegment(sketch, "E156.2", {"start": v(23.5, -15.16) * mm, "end": v(22.21, -17.37) * mm});
            skLineSegment(sketch, "E156.3", {"start": v(22.21, -17.37) * mm, "end": v(19.66, -17.37) * mm});
            skLineSegment(sketch, "E156.4", {"start": v(19.66, -17.37) * mm, "end": v(18.38, -15.16) * mm});
            skLineSegment(sketch, "E156.5", {"start": v(18.38, -15.16) * mm, "end": v(19.66, -12.94) * mm});
            skPoint(sketch, "E156.0.midPoint", {"position": v(20.93, -12.94) * mm});
            skSolve(sketch);
        }
        {
            var Q0;
            Q0 = qSketchRegion(id + "F45", true);
            extrude(context, id + "F46", {"entities" : qUnion([Q0]), "operationType" : NewBodyOperationType.ADD, "depth" : 3.3 * mm});
        }
        {
            var Q0;
            Q0=qCreatedBy(makeId("Top.planeOp"),FACE);
            var sketch = newSketch(context, id + "F47", { "sketchPlane" : qUnion([Q0])});
            skLineSegment(sketch, "E157.bottom", {"start": v(-34.78, -55.4) * mm, "end": v(34.78, -55.4) * mm});
            skLineSegment(sketch, "E157.top", {"start": v(-34.78, 55.4) * mm, "end": v(34.78, 55.4) * mm});
            skLineSegment(sketch, "E157.left", {"start": v(-34.78, -55.4) * mm, "end": v(-34.78, 55.4) * mm});
            skLineSegment(sketch, "E157.right", {"start": v(34.78, -55.4) * mm, "end": v(34.78, 55.4) * mm});
            skPoint(sketch, "E157.middle", {"position": v(0, 0) * mm});
            skSolve(sketch);
        }
        {
            var Q0;
            Q0 = qSketchRegion(id + "F47", true);
            extrude(context, id + "F48", {"entities" : qUnion([Q0]), "operationType" : NewBodyOperationType.REMOVE, "depth" : 77.98 * mm});
        }
    });
